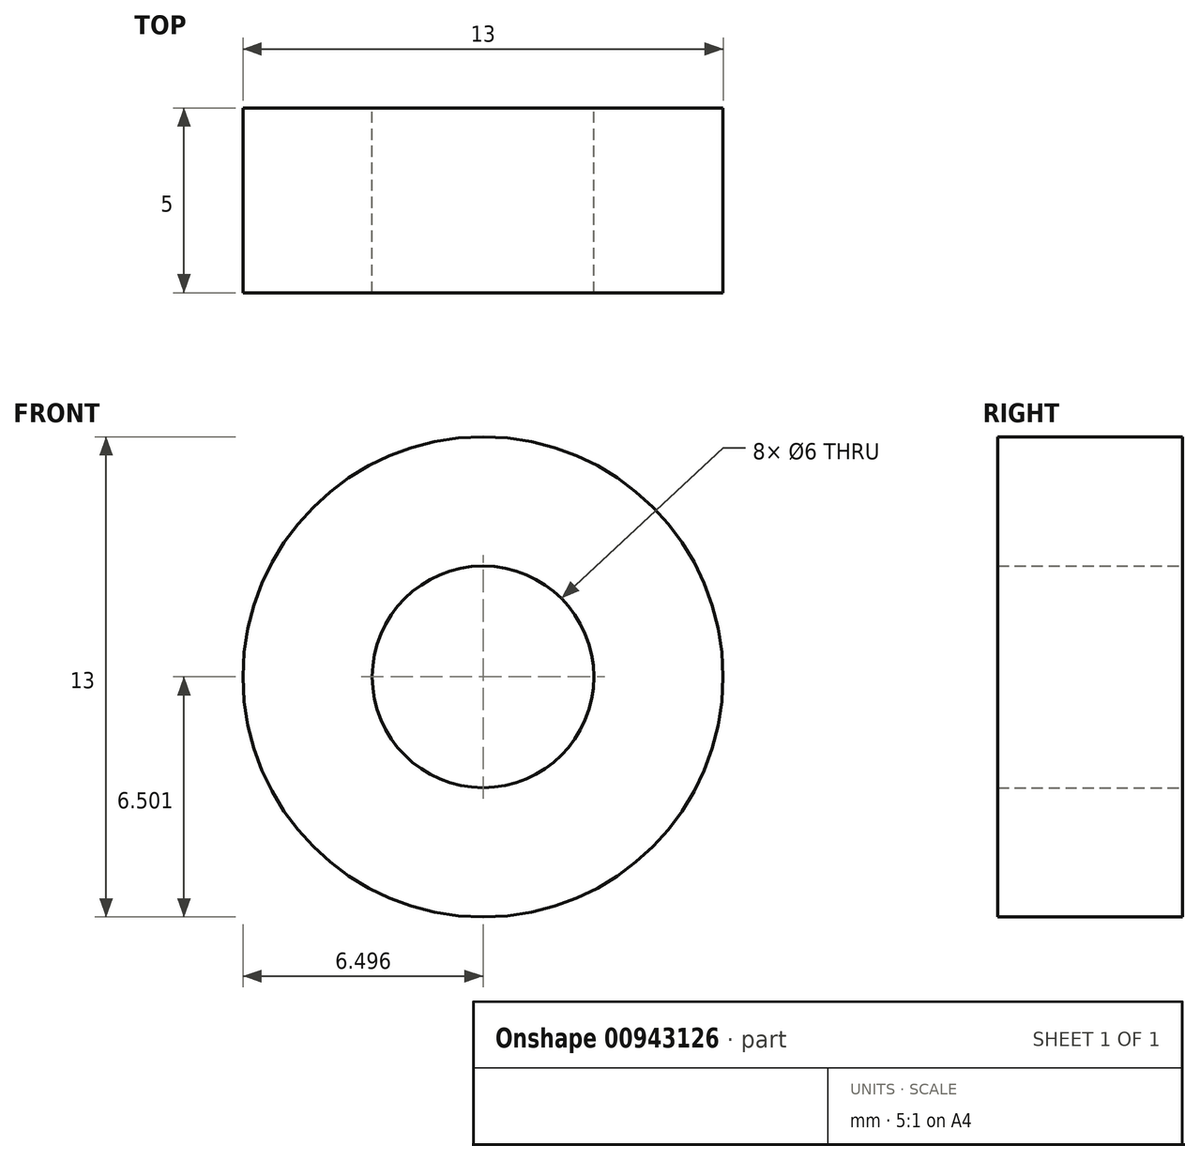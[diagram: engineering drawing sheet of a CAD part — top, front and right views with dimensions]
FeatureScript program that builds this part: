
annotation { "Feature Type Name" : "Feature", "Feature Type Description" : "" }
export const myFeature = defineFeature(function(context is Context, id is Id, definition is map)
    precondition{}
    {
        {
            var Q0;
            Q0=qCreatedBy(makeId("Front.planeOp"),FACE);
            var sketch = newSketch(context, id + "F0", { "sketchPlane" : qUnion([Q0])});
            skCircle(sketch, "E0", {"center": v(-28.7, 11.06) * mm, "radius": 3 * mm});
            skCircle(sketch, "E1", {"center": v(-28.7, 11.06) * mm, "radius": 6.5 * mm});
            skSolve(sketch);
        }
        {
            var Q0;
            Q0=qSketchRegion(id+"F0",true);
            extrude(context, id + "F1", {"entities" : qUnion([Q0]), "depth" : 5 * mm, "offsetDistance" : 25 * mm});
        }
    });
